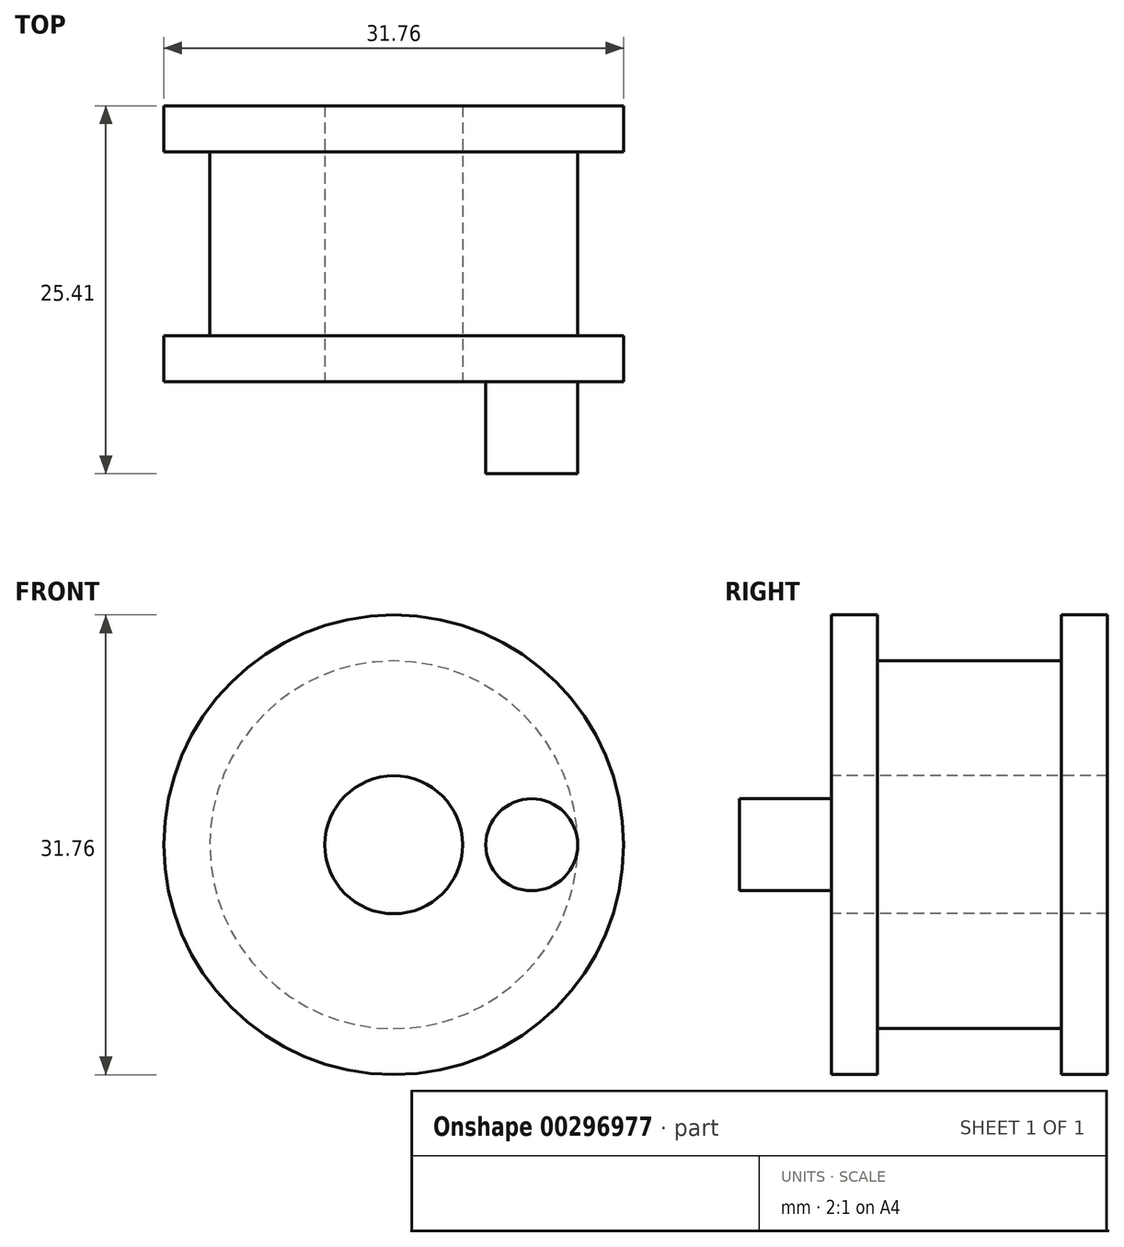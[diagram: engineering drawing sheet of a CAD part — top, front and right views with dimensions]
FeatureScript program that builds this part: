
annotation { "Feature Type Name" : "Feature", "Feature Type Description" : "" }
export const myFeature = defineFeature(function(context is Context, id is Id, definition is map)
    precondition{}
    {
        {
            var Q0;
            Q0=qCreatedBy(makeId("Right.planeOp"),FACE);
            var sketch = newSketch(context, id + "F0", { "sketchPlane" : qUnion([Q0])});
            skLineSegment(sketch, "E0.top", {"start": v(6.35, 4.76) * mm, "end": v(-6.35, 4.76) * mm});
            skPoint(sketch, "E0.middle", {"position": v(0, 0) * mm});
            skLineSegment(sketch, "E1.top", {"start": v(6.35, 12.7) * mm, "end": v(-6.35, 12.7) * mm});
            skLineSegment(sketch, "E1.left", {"start": v(6.35, 4.76) * mm, "end": v(6.35, 12.7) * mm});
            skLineSegment(sketch, "E1.right", {"start": v(-6.35, 4.76) * mm, "end": v(-6.35, 12.7) * mm});
            skPoint(sketch, "E1.middle", {"position": v(0, 8.73) * mm});
            skLineSegment(sketch, "E2.bottom", {"start": v(6.35, -12.7) * mm, "end": v(-6.35, -12.7) * mm});
            skLineSegment(sketch, "E2.top", {"start": v(6.35, -4.76) * mm, "end": v(-6.35, -4.76) * mm});
            skLineSegment(sketch, "E2.left", {"start": v(6.35, -12.7) * mm, "end": v(6.35, -4.76) * mm});
            skLineSegment(sketch, "E2.right", {"start": v(-6.35, -12.7) * mm, "end": v(-6.35, -4.76) * mm});
            skPoint(sketch, "E2.middle", {"position": v(0, -8.73) * mm});
            skLineSegment(sketch, "E3", {"start": v(-6.35, 4.76) * mm, "end": v(-9.53, 4.76) * mm});
            skLineSegment(sketch, "E4", {"start": v(-9.53, 4.76) * mm, "end": v(-9.53, 15.88) * mm});
            skLineSegment(sketch, "E5", {"start": v(-9.53, 15.87) * mm, "end": v(-6.35, 15.87) * mm});
            skLineSegment(sketch, "E6", {"start": v(-6.35, 15.88) * mm, "end": v(-6.35, 12.7) * mm});
            skLineSegment(sketch, "E7.bottom", {"start": v(6.35, -4.76) * mm, "end": v(9.53, -4.76) * mm});
            skLineSegment(sketch, "E7.top", {"start": v(6.35, -15.88) * mm, "end": v(9.52, -15.88) * mm});
            skLineSegment(sketch, "E7.left", {"start": v(6.35, -4.76) * mm, "end": v(6.35, -15.87) * mm});
            skLineSegment(sketch, "E7.right", {"start": v(9.53, -4.76) * mm, "end": v(9.53, -15.88) * mm});
            skLineSegment(sketch, "E8.bottom", {"start": v(6.35, 4.76) * mm, "end": v(9.52, 4.76) * mm});
            skLineSegment(sketch, "E8.top", {"start": v(6.35, 15.87) * mm, "end": v(9.52, 15.87) * mm});
            skLineSegment(sketch, "E8.left", {"start": v(6.35, 4.76) * mm, "end": v(6.35, 15.88) * mm});
            skLineSegment(sketch, "E8.right", {"start": v(9.53, 4.76) * mm, "end": v(9.53, 15.88) * mm});
            skLineSegment(sketch, "E9.bottom", {"start": v(-6.35, -4.76) * mm, "end": v(-9.53, -4.76) * mm});
            skLineSegment(sketch, "E9.top", {"start": v(-6.35, -15.88) * mm, "end": v(-9.52, -15.88) * mm});
            skLineSegment(sketch, "E9.left", {"start": v(-6.35, -4.76) * mm, "end": v(-6.35, -15.87) * mm});
            skLineSegment(sketch, "E9.right", {"start": v(-9.53, -4.76) * mm, "end": v(-9.52, -15.87) * mm});
            skLineSegment(sketch, "E10", {"start": v(-16, 0) * mm, "end": v(28.52, 0) * mm});
            skSolve(sketch);
        }
        {
            var Q0;
            Q0=makeQuery(id+"F0.imprint","IMPRINT",FACE,{"disambiguationData":[TD([[makeQuery(id+"F0.imprint","IMPRINT",EDGE,{"derivedFrom":sQuery(id+"F0.wireOp",EDGE,"E1.right")}),1.0]])]});
            var Q1;
            {var subQ0=sQuery(id+"F0.wireOp",EDGE,"E0.top");Q1=makeQuery(id+"F0.imprint","IMPRINT",FACE,{"disambiguationData":[TD([[makeQuery(id+"F0.imprint","IMPRINT",EDGE,{"derivedFrom":subQ0}),-1.0]])]});}
            var Q2;
            {var subQ3=sQuery(id+"F0.wireOp",EDGE,"E8.bottom");Q2=makeQuery(id+"F0.imprint","IMPRINT",FACE,{"disambiguationData":[TD([[makeQuery(id+"F0.imprint","IMPRINT",EDGE,{"derivedFrom":subQ3}),1.0]])]});}
            var Q3;
            Q3=sQuery(id+"F0.wireOp",EDGE,"E10");
            revolve(context, id + "F1", {"entities" : qUnion([Q0, Q1, Q2]), "axis" : qUnion([Q3]), "revolveType" : RevolveType.FULL});
        }
        {
            var Q0;
            Q0=makeQuery(id+"F1.opRevolve","SWEPT_FACE",FACE,{"disambiguationData":[OSD([sQuery(id+"F0.wireOp",EDGE,"E4")])]});
            var sketch = newSketch(context, id + "F2", { "sketchPlane" : qUnion([Q0])});
            skCircle(sketch, "E11", {"center": v(9.53, 0) * mm, "radius": 3.18 * mm});
            skSolve(sketch);
        }
        {
            var Q0;
            Q0=makeQuery(id+"F2.imprint","IMPRINT",FACE,{"disambiguationData":[TD([[makeQuery(id+"F2.imprint","IMPRINT",EDGE,{"derivedFrom":sQuery(id+"F2.wireOp",EDGE,"E11")}),1.0]])]});
            extrude(context, id + "F3", {"entities" : qUnion([Q0]), "operationType" : NewBodyOperationType.ADD, "depth" : 6.35 * mm});
        }
    });
